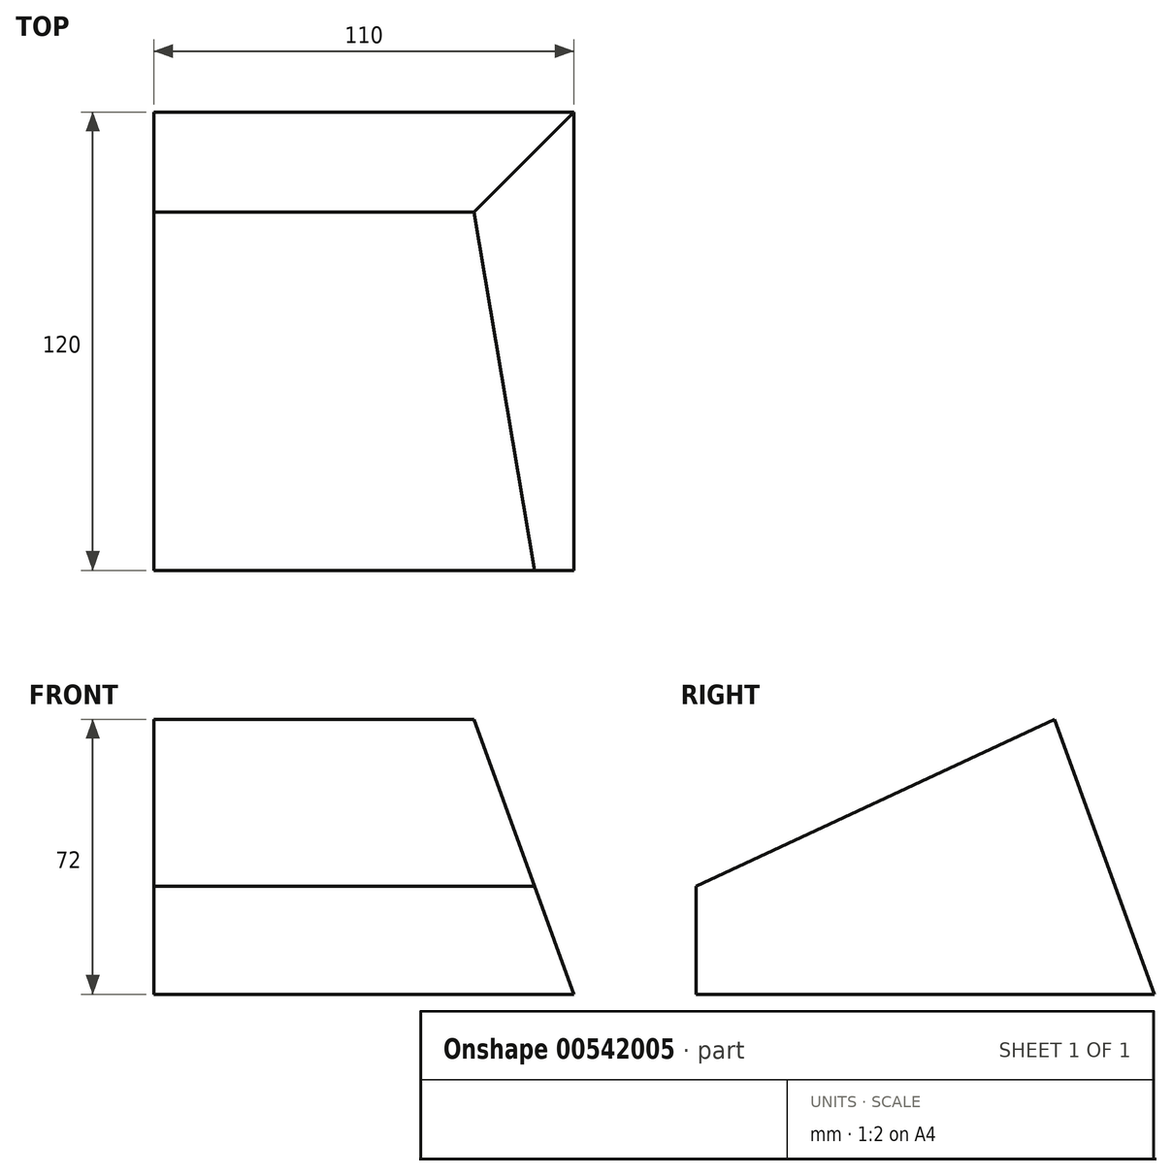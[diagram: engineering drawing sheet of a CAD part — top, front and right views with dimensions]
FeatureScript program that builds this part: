
annotation { "Feature Type Name" : "Feature", "Feature Type Description" : "" }
export const myFeature = defineFeature(function(context is Context, id is Id, definition is map)
    precondition{}
    {
        {
            var Q0;
            Q0=qCreatedBy(makeId("Top.planeOp"),FACE);
            var sketch = newSketch(context, id + "F0", { "sketchPlane" : qUnion([Q0])});
            skLineSegment(sketch, "E0.bottom", {"start": v(-110, 120) * mm, "end": v(0, 120) * mm});
            skLineSegment(sketch, "E0.top", {"start": v(-110, 0) * mm, "end": v(0, 0) * mm});
            skLineSegment(sketch, "E0.left", {"start": v(-110, 120) * mm, "end": v(-110, 0) * mm});
            skLineSegment(sketch, "E0.right", {"start": v(0, 120) * mm, "end": v(0, 0) * mm});
            skSolve(sketch);
        }
        {
            var Q0;
            Q0=makeQuery(id+"F0.imprint","IMPRINT",FACE,{"disambiguationData":[TD([[makeQuery(id+"F0.imprint","IMPRINT",EDGE,{"derivedFrom":sQuery(id+"F0.wireOp",EDGE,"E0.bottom")}),-1.0]])]});
            extrude(context, id + "F1", {"entities" : qUnion([Q0]), "depth" : 72 * mm, "offsetDistance" : 25 * mm});
        }
        {
            var Q0;
            Q0=makeQuery(id+"F1.opExtrude","SWEPT_FACE",FACE,{"disambiguationData":[OSD([sQuery(id+"F0.wireOp",EDGE,"E0.top")])]});
            var sketch = newSketch(context, id + "F2", { "sketchPlane" : qUnion([Q0])});
            skLineSegment(sketch, "E1", {"start": v(0, 0) * mm, "end": v(-26.2, 72) * mm});
            skLineSegment(sketch, "E2", {"start": v(-26.2, 72) * mm, "end": v(0, 72) * mm});
            skLineSegment(sketch, "E3", {"start": v(0, 72) * mm, "end": v(0, 0) * mm});
            skSolve(sketch);
        }
        {
            var Q0;
            Q0=makeQuery(id+"F2.imprint","IMPRINT",FACE,{"disambiguationData":[TD([[makeQuery(id+"F2.imprint","IMPRINT",EDGE,{"derivedFrom":sQuery(id+"F2.wireOp",EDGE,"E1")}),-1.0]])]});
            extrude(context, id + "F3", {"entities" : qUnion([Q0]), "operationType" : NewBodyOperationType.REMOVE, "oppositeDirection" : true, "depth" : 120 * mm, "offsetDistance" : 25 * mm});
        }
        {
            var Q0;
            Q0=qCreatedBy(makeId("Right.planeOp"),FACE);
            var sketch = newSketch(context, id + "F4", { "sketchPlane" : qUnion([Q0])});
            skLineSegment(sketch, "E4", {"start": v(120, 72) * mm, "end": v(93.8, 72) * mm});
            skLineSegment(sketch, "E5", {"start": v(93.8, 72) * mm, "end": v(120, 0) * mm});
            skLineSegment(sketch, "E6", {"start": v(120, 0) * mm, "end": v(120, 72) * mm});
            skSolve(sketch);
        }
        {
            var Q0;
            Q0=makeQuery(id+"F4.imprint","IMPRINT",FACE,{"disambiguationData":[TD([[makeQuery(id+"F4.imprint","IMPRINT",EDGE,{"derivedFrom":sQuery(id+"F4.wireOp",EDGE,"E4")}),1.0]])]});
            extrude(context, id + "F5", {"entities" : qUnion([Q0]), "operationType" : NewBodyOperationType.REMOVE, "oppositeDirection" : true, "depth" : 133 * mm, "offsetDistance" : 25 * mm});
        }
        {
            var Q0;
            Q0=qCreatedBy(makeId("Right.planeOp"),FACE);
            var sketch = newSketch(context, id + "F6", { "sketchPlane" : qUnion([Q0])});
            skLineSegment(sketch, "E7", {"start": v(93.8, 72) * mm, "end": v(0, 28.26) * mm});
            skLineSegment(sketch, "E8", {"start": v(0, 28.26) * mm, "end": v(0, 72) * mm});
            skLineSegment(sketch, "E9", {"start": v(0, 72) * mm, "end": v(93.8, 72) * mm});
            skSolve(sketch);
        }
        {
            var Q0;
            Q0 = qSketchRegion(id + "F6", true);
            extrude(context, id + "F7", {"entities" : qUnion([Q0]), "operationType" : NewBodyOperationType.REMOVE, "oppositeDirection" : true, "depth" : 133 * mm, "offsetDistance" : 25 * mm});
        }
    });
